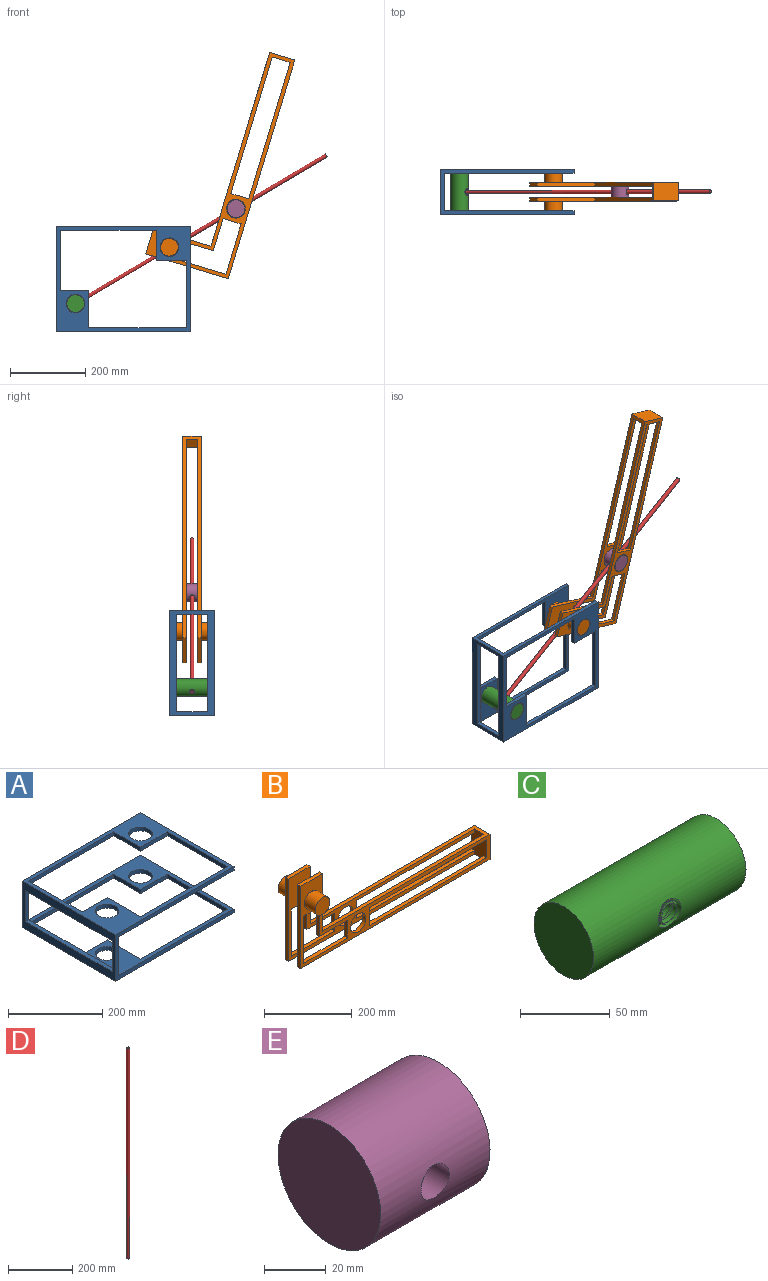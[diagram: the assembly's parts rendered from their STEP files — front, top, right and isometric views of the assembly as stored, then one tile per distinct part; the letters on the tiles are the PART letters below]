
ASSEMBLY  parts=5 mates=5
PART A: 32 faces, bbox 355x280x120 mm
  f0: plane 280x120mm, normal (-1,0,0), area 12800mm2, adj f3,f4,f6,f7,f28,f29,f30,f31
  f1: plane 280x120mm, normal (1,0,0), area 10400mm2, adj f3,f4,f6,f7,f8,f9,f14,f20
  f2: plane 280x10mm, normal (1,0,0), area 2800mm2, adj f3,f4,f6,f9
  f3: plane 355x120mm, normal (0,1,0), area 8100mm2, adj f0,f1,f2,f5,f6,f7,f8,f9
  f4: plane 355x120mm, normal (0,-1,0), area 8100mm2, adj f0,f1,f2,f5,f6,f7,f8,f9
  f5: plane 280x10mm, normal (1,0,0), area 2800mm2, adj f3,f4,f7,f8
  f6: plane 355x280mm, normal (0,0,1), area 22273mm2, adj f0,f1,f2,f3,f4,f10,f11,f14
  f7: plane 355x280mm, normal (0,0,-1), area 22273mm2, adj f0,f1,f3,f4,f5,f12,f13,f21
  f8: plane 345x280mm, normal (0,0,1), area 19473mm2, adj f1,f3,f4,f5,f12,f13,f21,f22
  f9: plane 345x280mm, normal (0,0,-1), area 19473mm2, adj f1,f2,f3,f4,f10,f11,f14,f15
  f10: cylinder r=25mm len=50mm, axis (0,0,1), area 1570.8mm2, adj f6,f9
  f11: cylinder r=25mm len=50mm, axis (0,0,1), area 1570.8mm2, adj f6,f9
  f12: cylinder r=25mm len=50mm, axis (0,0,1), area 1570.8mm2, adj f7,f8
  f13: cylinder r=25mm len=50mm, axis (0,0,1), area 1570.8mm2, adj f7,f8
  f14: plane 255x10mm, normal (0,-1,0), area 2550mm2, adj f1,f6,f9,f15
  f15: plane 80x10mm, normal (-1,0,0), area 800mm2, adj f6,f9,f14,f16
  f16: plane 80x10mm, normal (0,-1,0), area 800mm2, adj f6,f9,f15,f17
  f17: plane 180x10mm, normal (-1,0,0), area 1800mm2, adj f6,f9,f16,f18
  f18: plane 260x10mm, normal (0,1,0), area 2600mm2, adj f6,f9,f17,f19
  f19: plane 100x10mm, normal (1,0,0), area 1000mm2, adj f6,f9,f18,f20
  f20: plane 75x10mm, normal (0,1,0), area 750mm2, adj f1,f6,f9,f19
  f21: plane 75x10mm, normal (0,1,0), area 750mm2, adj f1,f7,f8,f22
  f22: plane 100x10mm, normal (1,0,0), area 1000mm2, adj f7,f8,f21,f23
  f23: plane 260x10mm, normal (0,1,0), area 2600mm2, adj f7,f8,f22,f24
  f24: plane 180x10mm, normal (-1,0,0), area 1800mm2, adj f7,f8,f23,f25
  f25: plane 80x10mm, normal (0,-1,0), area 800mm2, adj f7,f8,f24,f26
  f26: plane 80x10mm, normal (-1,0,0), area 800mm2, adj f7,f8,f25,f27
  f27: plane 255x10mm, normal (0,-1,0), area 2550mm2, adj f1,f7,f8,f26
  f28: plane 80x10mm, normal (0,-1,0), area 800mm2, adj f0,f1,f29,f31
  f29: plane 260x10mm, normal (0,0,-1), area 2600mm2, adj f0,f1,f28,f30
  f30: plane 80x10mm, normal (0,1,0), area 800mm2, adj f0,f1,f29,f31
  f31: plane 260x10mm, normal (0,0,1), area 2600mm2, adj f0,f1,f28,f30
PART B: 38 faces, bbox 610x120x230 mm
  f0: plane 610x230mm, normal (0,-1,0), area 20126.6mm2, adj f4,f7,f9,f10,f11,f12,f13,f17
  f1: plane 610x230mm, normal (0,1,0), area 20126.6mm2, adj f5,f6,f7,f8,f9,f10,f15,f17
  f2: plane 600x230mm, normal (0,-1,0), area 21161.5mm2, adj f5,f6,f7,f8,f9,f17,f19,f29
  f3: plane 600x230mm, normal (0,1,0), area 21161.5mm2, adj f4,f7,f9,f11,f12,f17,f18,f20
  f4: plane 230x10mm, normal (-1,0,0), area 2300mm2, adj f0,f3,f9,f12
  f5: plane 70x10mm, normal (0,0,1), area 700mm2, adj f1,f2,f6,f8
  f6: plane 230x10mm, normal (-1,0,0), area 2300mm2, adj f1,f2,f5,f9
  f7: plane 540x50mm, normal (0,0,1), area 11100mm2, adj f0,f1,f2,f3,f8,f10,f11,f17
  f8: plane 160x10mm, normal (1,0,0), area 1600mm2, adj f1,f2,f5,f7
  f9: plane 610x50mm, normal (0,0,-1), area 12500mm2, adj f0,f1,f2,f3,f4,f6,f10,f17
  f10: plane 70x50mm, normal (1,0,0), area 3500mm2, adj f0,f1,f7,f9
  f11: plane 160x10mm, normal (1,0,0), area 1600mm2, adj f0,f3,f7,f12
  f12: plane 70x10mm, normal (0,0,1), area 700mm2, adj f0,f3,f4,f11
  f13: cylinder r=23.5mm len=47mm, axis (0,1,0), area 5167.9mm2, adj f0,f14
  f14: plane 47x47mm, normal (0,-1,0), area 1734.9mm2, adj f13
  f15: cylinder r=23.5mm len=47mm, axis (0,-1,0), area 5167.9mm2, adj f1,f16
  f16: plane 47x47mm, normal (0,1,0), area 1734.9mm2, adj f15
  f17: plane 70x50mm, normal (-1,0,0), area 3100mm2, adj f0,f1,f2,f3,f7,f9,f26,f28
  f18: cylinder r=25mm len=50mm, axis (0,-1,0), area 1570.8mm2, adj f0,f3
  f19: cylinder r=25mm len=50mm, axis (0,-1,0), area 1570.8mm2, adj f1,f2
  f20: plane 50x10mm, normal (-1,0,0), area 500mm2, adj f0,f3,f21,f25
  f21: plane 140x10mm, normal (0,0,1), area 1400mm2, adj f0,f3,f20,f22
  f22: plane 131.5x10mm, normal (1,0,0), area 1315mm2, adj f0,f3,f21,f23
  f23: plane 50x10mm, normal (0,0,-1), area 500mm2, adj f0,f3,f22,f24
  f24: plane 81.5x10mm, normal (-1,0,0), area 815mm2, adj f0,f3,f23,f25
  f25: plane 90x10mm, normal (0,0,-1), area 900mm2, adj f0,f3,f20,f24
  f26: plane 380x10mm, normal (0,0,1), area 3800mm2, adj f0,f3,f17,f27
  f27: plane 50x10mm, normal (1,0,0), area 500mm2, adj f0,f3,f26,f28
  f28: plane 380x10mm, normal (0,0,-1), area 3800mm2, adj f0,f3,f17,f27
  f29: plane 90x10mm, normal (0,0,-1), area 900mm2, adj f1,f2,f30,f34
  f30: plane 81.5x10mm, normal (-1,0,0), area 815mm2, adj f1,f2,f29,f31
  f31: plane 50x10mm, normal (0,0,-1), area 500mm2, adj f1,f2,f30,f32
  f32: plane 131.5x10mm, normal (1,0,0), area 1315mm2, adj f1,f2,f31,f33
  f33: plane 140x10mm, normal (0,0,1), area 1400mm2, adj f1,f2,f32,f34
  f34: plane 50x10mm, normal (-1,0,0), area 500mm2, adj f1,f2,f29,f33
  f35: plane 380x10mm, normal (0,0,-1), area 3800mm2, adj f1,f2,f17,f36
  f36: plane 50x10mm, normal (1,0,0), area 500mm2, adj f1,f2,f35,f37
  f37: plane 380x10mm, normal (0,0,1), area 3800mm2, adj f1,f2,f17,f36
PART C: 18 faces, bbox 120x48.7x47 mm
  f0: cylinder r=23.5mm len=120mm, axis (-1,0,0), area 17326.1mm2, adj f1,f11,f12,f13
  f1: cylinder r=6.5mm len=13mm, axis (0,1,0), area 373.7mm2, adj f0,f2,f14,f15,f16
  f2: cylinder r=6.5mm len=13mm, axis (0,1,0), area 132.8mm2, adj f1,f3,f15,f16
  f3: cylinder r=6.5mm len=13mm, axis (0,1,0), area 132.8mm2, adj f2,f4,f15,f16
  f4: cylinder r=6.5mm len=13mm, axis (0,1,0), area 132.8mm2, adj f3,f5,f15,f16
  f5: cylinder r=6.5mm len=13mm, axis (0,1,0), area 132.8mm2, adj f4,f6,f15,f16
  f6: cylinder r=6.5mm len=13mm, axis (0,1,0), area 132.8mm2, adj f5,f7,f15,f16
  f7: cylinder r=6.5mm len=13mm, axis (0,1,0), area 132.8mm2, adj f6,f8,f15,f16
  f8: cylinder r=6.5mm len=13mm, axis (0,1,0), area 129.1mm2, adj f7,f9,f10,f15,f16
  f9: cylinder r=6.5mm len=12.36mm, axis (0,1,0), area 17.2mm2, adj f8,f10,f16
  f10: cylinder r=23.5mm len=13.46mm, axis (-1,0,0), area 23.3mm2, adj f8,f9,f15,f16
  f11: plane 47x47mm, normal (1,0,0), area 1734.9mm2, adj f0
  f12: plane 47x47mm, normal (-1,0,0), area 1734.9mm2, adj f0
  f13: cylinder r=8.98mm len=41.22mm, axis (0,1,0), area 2185.7mm2, adj f0,f14,f17
  f14: plane 6.01x3.66mm, normal (0.6,0,0.8), area 18.2mm2, adj f1,f13,f15,f16,f17
  f15: bspline ~42.41x15.26mm, area 691mm2, adj f1,f2,f3,f4,f5,f6,f7,f8
  f16: bspline ~41.67x17.79mm, area 766.8mm2, adj f1,f2,f3,f4,f5,f6,f7,f8
  f17: bspline ~20.58x19.11mm, area 77mm2, adj f13,f14,f15
PART D: 3 faces, bbox 10x10x800 mm
  f0: cylinder r=5mm len=800mm, axis (0,0,-1), area 25132.7mm2, adj f1,f2
  f1: plane 10x10mm, normal (0,0,1), area 78.5mm2, adj f0
  f2: plane 10x10mm, normal (0,0,-1), area 78.5mm2, adj f0
PART E: 4 faces, bbox 50x47x47 mm
  f0: cylinder r=23.5mm len=50mm, axis (1,0,0), area 7114.4mm2, adj f1,f2,f3
  f1: plane 47x47mm, normal (-1,0,0), area 1734.9mm2, adj f0
  f2: cylinder r=6.5mm len=47mm, axis (0,1,0), area 1882.3mm2, adj f0
  f3: plane 47x47mm, normal (1,0,0), area 1734.9mm2, adj f0
PLACE A rot(axis=(1,0,0),90deg) t=(-112.5,388.97,-126.47)mm fixed
PLACE B rot(axis=(0,-1,0),73.1deg) t=(344.79,353.97,14.2)mm
PLACE C rot(axis=(-0.26,-0.26,0.93),94deg) t=(-140.33,278.97,-155.59)mm
PLACE D rot(axis=(0,1,0),59.4deg) t=(-82.97,328.97,-63.58)mm
PLACE E rot(axis=(0.26,-0.26,-0.93),94deg) t=(524.7,353.97,226.11)mm
MATE revolute E.f0 <-> B.f18  axis (0,-1,0) through (365.04,303.97,201.39)mm
MATE revolute C.f0 <-> A.f11  axis (0,-1,0) through (-62.5,268.97,-51.47)mm
MATE revolute D.f0 <-> C.f1  axis (-0.86,0,-0.51) through (-82.97,328.97,-63.58)mm
MATE slider D.f0 <-> E.f2  axis (-0.86,0,-0.51) through (261.32,328.97,140.05)mm
MATE revolute B.f13 <-> A.f10  axis (0,-1,0) through (187.5,268.97,98.53)mm
